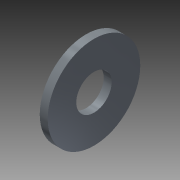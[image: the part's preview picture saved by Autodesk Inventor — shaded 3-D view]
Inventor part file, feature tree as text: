
AUTODESK INVENTOR PART (.ipt)
format: ipt  version: 2014 (Build 180170000, 170)  size: 102,400 bytes
history: native  units: mm (DEFAULTED — no unit token found)
features: other x1, plane x1, sketch x1
ambient origin geometry x7: Origin, YZ Plane, XY Plane, X Axis, Y Axis, Z Axis, Center Point
bodies: Solid1 (feature_tree), Body (feature_tree)
feature tree (3):
  other  "Work Axis1"
  plane  "Work Plane1"
  sketch  "Sketch"  dims[d0=7.1374mm d1=18.6436mm d2=1.6002mm d3=0.0mm d4=0.0mm d5=0.0mm d6=0.0mm d7=0.0mm]
